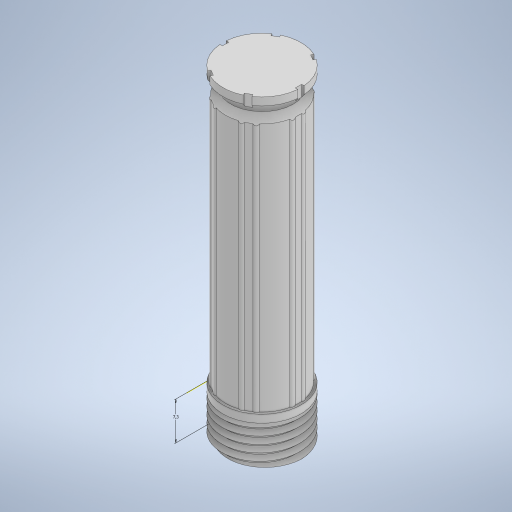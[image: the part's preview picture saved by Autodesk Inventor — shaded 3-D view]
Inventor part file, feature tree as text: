
AUTODESK INVENTOR PART (.ipt)
format: ipt  version: 2024 (Build 280153000, 153)  size: 545,280 bytes
history: native  units: mm
features: sketch x9, extrude x6, pattern_circular x2, other x1, revolve x1, fillet x1
ambient origin geometry x8: Origin, YZ Plane, XZ Plane, XY Plane, X Axis, Y Axis, Z Axis, Center Point
bodies: Volumenkörper1 (feature_tree)
feature tree (20):
  extrude  "Extrusion1"  Depth=61.8mm TaperAngle=0.0deg
  other  "Spirale1"
  extrude  "Extrusion9"  Depth=3.5mm
  revolve  "Umdrehung1"
  extrude  "Extrusion6"  Depth=2.0mm
  pattern_circular  "Runde Anordnung1"  Count=4  [1 undecoded]
  extrude  "Extrusion7"  Depth=1.0mm
  pattern_circular  "Runde Anordnung2"  Count=6 Angle=360.0deg
  extrude  "Extrusion8"  Depth=0.65mm
  extrude  "Extrusion10"  Depth=0.65mm
  fillet  "Rundung6"  Radius=1.4mm
  sketch  "Skizze16"  dims[d43=27.0mm d44=21.85mm d45=0.0mm d46=0.0mm d47=60.0mm d48=360.0deg d51=1.0mm d54=15.0mm d56=1.4mm d58=1.4mm d59=9.85mm d60=10.0mm d61=0.0mm d62=90.0deg d63=90.0deg d64=0.0mm d65=0.0mm d66=1.5mm d67=0.0mm d68=15.0mm d69=52.8mm d70=0.0mm d71=60.0deg d72=0.2mm d73=7.5mm d74=15.0mm d75=14.5mm d76=15.0mm d77=27.0mm d78=21.85mm d79=0.0mm d80=0.0mm d82=0.65mm d83=7.29974mm d52=0.0mm d53=0.0mm d55=0.0mm]
  sketch  "Skizze1"  dims[d0=15.0mm d1=61.8mm d2=0.0mm]
  sketch  "Skizze6"  dims[d20=1.5mm d21=3.5mm]
  sketch  "Skizze8"  dims[d22=2.0mm d23=2.0mm]
  sketch  "Skizze9"  dims[d24=90.0deg]
  sketch  "Skizze12"  dims[d32=0.5mm]
  sketch  "Skizze13"  dims[d33=0.6mm]
  sketch  "Skizze14"  dims[d34=0.6mm d35=40.0mm d36=21.85mm d37=0.0mm d38=0.0mm]
  sketch  "Skizze15"  dims[d39=60.0mm d40=360.0deg d42=1.0mm]
note: 1 required parameter value undecoded (feature->parameter linkage not recoverable at this tier; creation-order binding heuristic only, values carry confidence <= 0.55)
